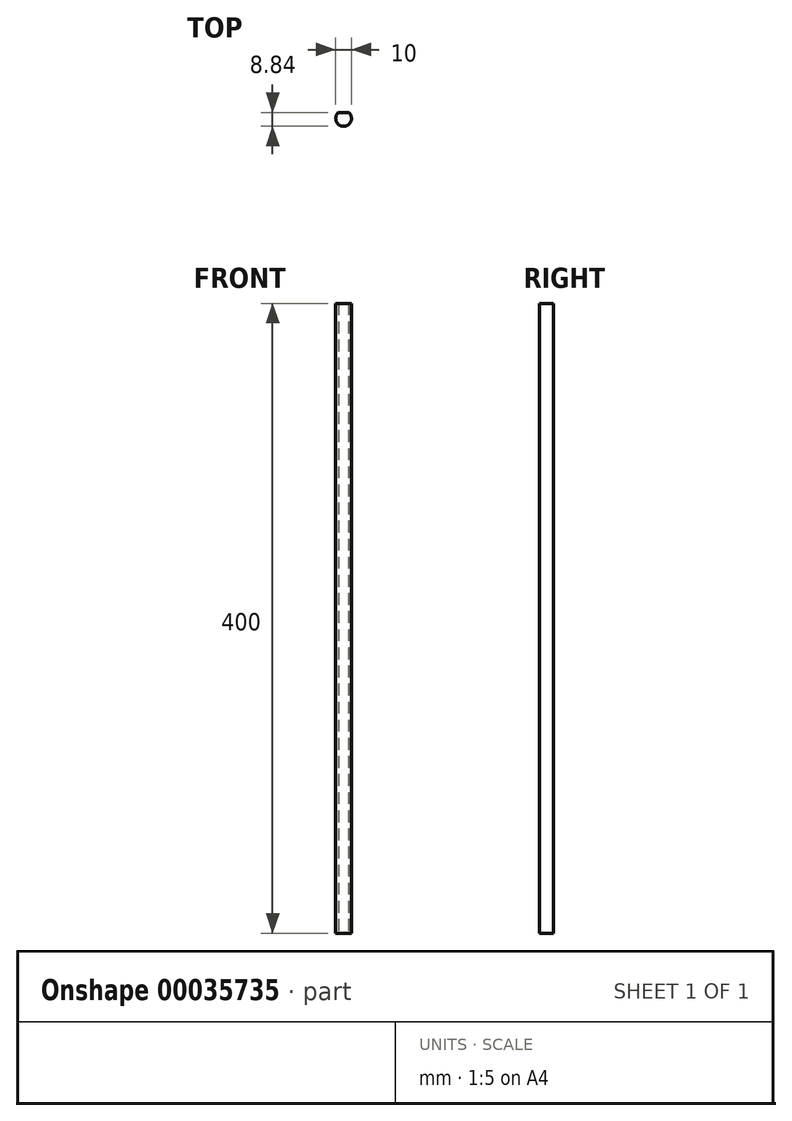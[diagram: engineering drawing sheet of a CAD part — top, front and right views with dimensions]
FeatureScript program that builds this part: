
annotation { "Feature Type Name" : "Feature", "Feature Type Description" : "" }
export const myFeature = defineFeature(function(context is Context, id is Id, definition is map)
    precondition{}
    {
        {
            var Q0;
            Q0=qCreatedBy(makeId("Top.planeOp"),FACE);
            var sketch = newSketch(context, id + "F0", { "sketchPlane" : qUnion([Q0])});
            skArc(sketch, "E0", {"start": v(-3.2, 3.84) * mm, "mid": v(0, -5) * mm, "end": v(3.2, 3.84) * mm});
            skLineSegment(sketch, "E1", {"start": v(-3.2, 3.84) * mm, "end": v(3.2, 3.84) * mm});
            skSolve(sketch);
        }
        {
            var Q0;
            Q0=makeQuery(id+"F0.imprint","IMPRINT",FACE,{"disambiguationData":[TD([[makeQuery(id+"F0.imprint","IMPRINT",EDGE,{"derivedFrom":sQuery(id+"F0.wireOp",EDGE,"E0")}),1.0]])]});
            extrude(context, id + "F1", {"entities" : qUnion([Q0]), "depth" : 400 * mm});
        }
    });
